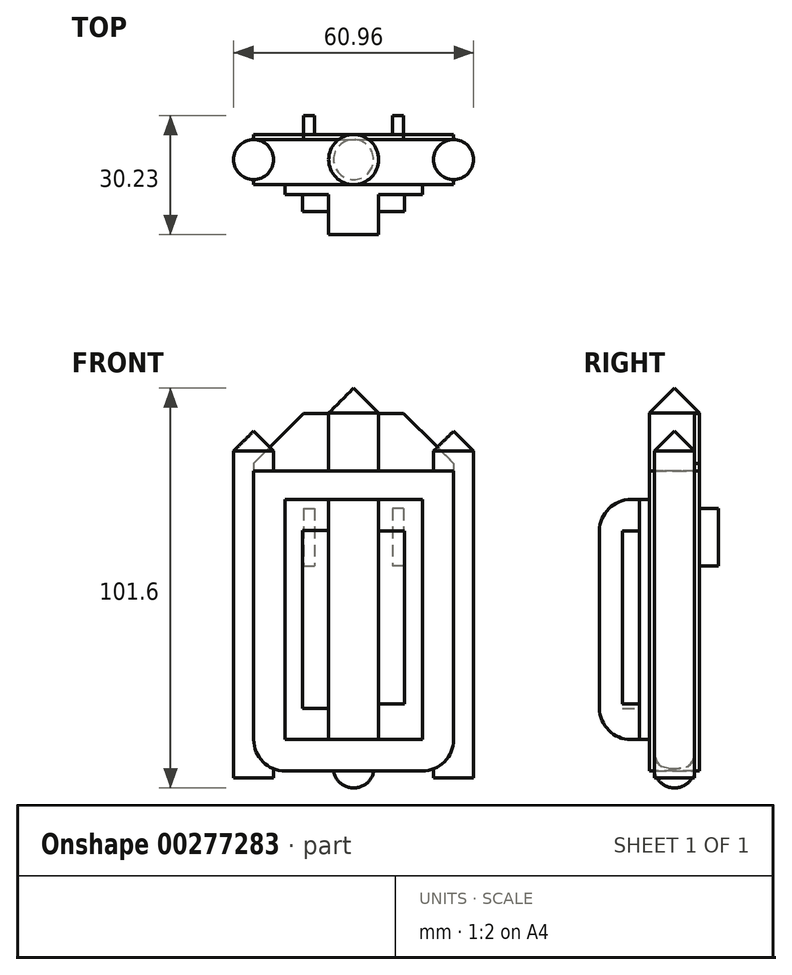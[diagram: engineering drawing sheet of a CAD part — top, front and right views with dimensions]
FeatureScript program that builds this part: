
annotation { "Feature Type Name" : "Feature", "Feature Type Description" : "" }
export const myFeature = defineFeature(function(context is Context, id is Id, definition is map)
    precondition{}
    {
        {
            var Q0;
            Q0=qCreatedBy(makeId("Front.planeOp"),FACE);
            var sketch = newSketch(context, id + "F0", { "sketchPlane" : qUnion([Q0])});
            skLineSegment(sketch, "E0.bottom", {"start": v(-23.73, -37.34) * mm, "end": v(27.07, -37.34) * mm});
            skLineSegment(sketch, "E0.top", {"start": v(-23.73, 38.86) * mm, "end": v(27.07, 38.86) * mm});
            skLineSegment(sketch, "E0.left", {"start": v(-23.73, -37.34) * mm, "end": v(-23.73, 38.86) * mm});
            skLineSegment(sketch, "E0.right", {"start": v(27.07, -37.34) * mm, "end": v(27.07, 38.86) * mm});
            skSolve(sketch);
        }
        {
            var Q0;
            Q0 = qSketchRegion(id + "F0", true);
            extrude(context, id + "F1", {"entities" : qUnion([Q0]), "depth" : 12.7 * mm});
        }
        {
            var Q0;
            Q0=makeQuery(id+"F1.opExtrude","SWEPT_EDGE",EDGE,{"disambiguationData":[OSD([sQuery(id+"F0.wireOp",EDGE,"E0.bottom"),sQuery(id+"F0.wireOp",EDGE,"E0.left")])]});
            var Q1;
            Q1=makeQuery(id+"F1.opExtrude","SWEPT_EDGE",EDGE,{"disambiguationData":[OSD([sQuery(id+"F0.wireOp",EDGE,"E0.bottom"),sQuery(id+"F0.wireOp",EDGE,"E0.right")])]});
            fillet(context, id + "F2", {"entities" : qUnion([Q0, Q1]), "radius" : 7.97 * mm, "tangentPropagation" : true, "allowEdgeOverflow" : false});
        }
        {
            var Q0;
            Q0=makeQuery(id+"F1.opExtrude","CAP_FACE",FACE,{"disambiguationData":[OSD([sQuery(id+"F0.wireOp",EDGE,"E0.bottom"),sQuery(id+"F0.wireOp",EDGE,"E0.top"),sQuery(id+"F0.wireOp",EDGE,"E0.left"),sQuery(id+"F0.wireOp",EDGE,"E0.right")])],"isStart":false});
            var sketch = newSketch(context, id + "F3", { "sketchPlane" : qUnion([Q0])});
            skLineSegment(sketch, "E1", {"start": v(-15.76, -29.36) * mm, "end": v(19.1, -29.36) * mm});
            skLineSegment(sketch, "E2", {"start": v(19.1, -29.36) * mm, "end": v(19.1, 31.64) * mm});
            skLineSegment(sketch, "E3", {"start": v(19.1, 31.64) * mm, "end": v(-15.76, 31.64) * mm});
            skLineSegment(sketch, "E4", {"start": v(-15.76, 31.64) * mm, "end": v(-15.76, -29.36) * mm});
            skSolve(sketch);
        }
        {
            var Q0;
            Q0 = qSketchRegion(id + "F3", true);
            extrude(context, id + "F4", {"entities" : qUnion([Q0]), "operationType" : NewBodyOperationType.ADD, "depth" : 2.54 * mm});
        }
        {
            var Q0;
            Q0=makeQuery(id+"F1.opExtrude","SWEPT_FACE",FACE,{"disambiguationData":[OSD([sQuery(id+"F0.wireOp",EDGE,"E0.top")])]});
            var sketch = newSketch(context, id + "F5", { "sketchPlane" : qUnion([Q0])});
            skCircle(sketch, "E5", {"center": v(-23.73, -6.35) * mm, "radius": 5.08 * mm});
            skPoint(sketch, "E6.centerSnap0", {"position": v(1.67, 0) * mm});
            skCircle(sketch, "E7", {"center": v(27.07, -6.35) * mm, "radius": 5.08 * mm});
            skSolve(sketch);
        }
        {
            var Q0;
            {var subQ0=sQuery(id+"F5.wireOp",EDGE,"E5");var subQ1=makeQuery(id+"F1.opExtrude","SWEPT_EDGE",EDGE,{"disambiguationData":[OSD([sQuery(id+"F0.wireOp",EDGE,"E0.top"),sQuery(id+"F0.wireOp",EDGE,"E0.left")])]});var subQ2=makeQuery(id+"F5.imprint","INTERSECT",VERTEX,{"disambiguationData":[OD(0.0)],"derivedFrom":[subQ1,subQ0]});Q0=makeQuery(id+"F5.imprint","IMPRINT",FACE,{"disambiguationData":[TD([[makeQuery(id+"F5.imprint","IMPRINT",EDGE,{"disambiguationData":[TD([[subQ2,-1.0]])],"derivedFrom":subQ0}),1.0]])]});}
            var Q1;
            {var subQ0=sQuery(id+"F5.wireOp",EDGE,"E7");var subQ1=makeQuery(id+"F1.opExtrude","SWEPT_EDGE",EDGE,{"disambiguationData":[OSD([sQuery(id+"F0.wireOp",EDGE,"E0.top"),sQuery(id+"F0.wireOp",EDGE,"E0.right")])]});var subQ2=makeQuery(id+"F5.imprint","INTERSECT",VERTEX,{"disambiguationData":[OD(0.0)],"derivedFrom":[subQ1,subQ0]});Q1=makeQuery(id+"F5.imprint","IMPRINT",FACE,{"disambiguationData":[TD([[makeQuery(id+"F5.imprint","IMPRINT",EDGE,{"disambiguationData":[TD([[subQ2,1.0]])],"derivedFrom":subQ0}),1.0]])]});}
            var Q2;
            {var subQ0=sQuery(id+"F5.wireOp",EDGE,"E5");var subQ1=makeQuery(id+"F1.opExtrude","SWEPT_EDGE",EDGE,{"disambiguationData":[OSD([sQuery(id+"F0.wireOp",EDGE,"E0.top"),sQuery(id+"F0.wireOp",EDGE,"E0.left")])]});var subQ2=makeQuery(id+"F5.imprint","INTERSECT",VERTEX,{"disambiguationData":[OD(0.0)],"derivedFrom":[subQ1,subQ0]});Q2=makeQuery(id+"F5.imprint","IMPRINT",FACE,{"disambiguationData":[TD([[makeQuery(id+"F5.imprint","IMPRINT",EDGE,{"disambiguationData":[TD([[subQ2,1.0]])],"derivedFrom":subQ0}),1.0]])]});}
            var Q3;
            {var subQ0=sQuery(id+"F5.wireOp",EDGE,"E7");var subQ1=makeQuery(id+"F1.opExtrude","SWEPT_EDGE",EDGE,{"disambiguationData":[OSD([sQuery(id+"F0.wireOp",EDGE,"E0.top"),sQuery(id+"F0.wireOp",EDGE,"E0.right")])]});var subQ2=makeQuery(id+"F5.imprint","INTERSECT",VERTEX,{"disambiguationData":[OD(0.0)],"derivedFrom":[subQ1,subQ0]});Q3=makeQuery(id+"F5.imprint","IMPRINT",FACE,{"disambiguationData":[TD([[makeQuery(id+"F5.imprint","IMPRINT",EDGE,{"disambiguationData":[TD([[subQ2,-1.0]])],"derivedFrom":subQ0}),1.0]])]});}
            extrude(context, id + "F6", {"entities" : qUnion([Q0, Q1, Q2, Q3]), "operationType" : NewBodyOperationType.ADD, "oppositeDirection" : true, "depth" : 77.98 * mm});
        }
        {
            var Q0;
            Q0=makeQuery(id+"F6.boolean.opBoolean","MERGE",FACE,{"derivedFrom":[makeQuery(id+"F1.opExtrude","SWEPT_FACE",FACE,{"disambiguationData":[OSD([sQuery(id+"F0.wireOp",EDGE,"E0.top")])]}),makeQuery(id+"F6.opExtrude","CAP_FACE",FACE,{"disambiguationData":[OSD([sQuery(id+"F5.wireOp",EDGE,"E5")])],"isStart":true}),makeQuery(id+"F6.opExtrude","CAP_FACE",FACE,{"disambiguationData":[OSD([sQuery(id+"F5.wireOp",EDGE,"E7")])],"isStart":true})]});
            var sketch = newSketch(context, id + "F7", { "sketchPlane" : qUnion([Q0])});
            skCircle(sketch, "E8", {"center": v(1.67, -6.35) * mm, "radius": 6.35 * mm});
            skPoint(sketch, "E8.centerSnap0", {"position": v(1.67, 0) * mm});
            skPoint(sketch, "E8.centerSnap1", {"position": v(-28.8, -6.35) * mm});
            skSolve(sketch);
        }
        {
            var Q0;
            Q0 = qSketchRegion(id + "F7", true);
            extrude(context, id + "F8", {"entities" : qUnion([Q0]), "operationType" : NewBodyOperationType.ADD, "depth" : 21.08 * mm});
        }
        {
            var Q0;
            Q0=makeQuery(id+"F8.opExtrude","CAP_EDGE",EDGE,{"disambiguationData":[OSD([sQuery(id+"F7.wireOp",EDGE,"E8")])],"isStart":false});
            chamfer(context, id + "F9", {"entities" : qUnion([Q0]), "width" : 6.35 * mm, "tangentPropagation" : true});
        }
        {
            var Q0;
            Q0=makeQuery(id+"F4.opExtrude","CAP_FACE",FACE,{"disambiguationData":[OSD([sQuery(id+"F3.wireOp",EDGE,"E1"),sQuery(id+"F3.wireOp",EDGE,"E2"),sQuery(id+"F3.wireOp",EDGE,"E3"),sQuery(id+"F3.wireOp",EDGE,"E4")])],"isStart":false});
            var sketch = newSketch(context, id + "F10", { "sketchPlane" : qUnion([Q0])});
            skLineSegment(sketch, "E9", {"start": v(1.67, 31.64) * mm, "end": v(-4.68, 31.64) * mm});
            skLineSegment(sketch, "E10", {"start": v(1.67, 31.64) * mm, "end": v(8.02, 31.64) * mm});
            skLineSegment(sketch, "E11", {"start": v(-4.68, 31.64) * mm, "end": v(-4.68, -29.36) * mm});
            skLineSegment(sketch, "E12", {"start": v(-4.68, -29.36) * mm, "end": v(8.02, -29.36) * mm});
            skLineSegment(sketch, "E13", {"start": v(8.02, -29.36) * mm, "end": v(8.02, 31.64) * mm});
            skSolve(sketch);
        }
        {
            var Q0;
            Q0 = qSketchRegion(id + "F10", true);
            extrude(context, id + "F11", {"entities" : qUnion([Q0]), "operationType" : NewBodyOperationType.ADD, "depth" : 10.16 * mm});
        }
        {
            var Q0;
            Q0=makeQuery(id+"F11.opExtrude","CAP_EDGE",EDGE,{"disambiguationData":[OSD([sQuery(id+"F10.wireOp",EDGE,"E9"),sQuery(id+"F10.wireOp",EDGE,"E10")])],"isStart":false});
            var Q1;
            Q1=makeQuery(id+"F11.opExtrude","CAP_EDGE",EDGE,{"disambiguationData":[OSD([sQuery(id+"F10.wireOp",EDGE,"E12")])],"isStart":false});
            fillet(context, id + "F12", {"entities" : qUnion([Q0, Q1]), "radius" : 7.97 * mm, "tangentPropagation" : true, "allowEdgeOverflow" : false});
        }
        {
            var Q0;
            Q0 = qSketchRegion(id + "F5", true);
            extrude(context, id + "F13", {"entities" : qUnion([Q0]), "operationType" : NewBodyOperationType.ADD, "depth" : 10.16 * mm});
        }
        {
            var Q0;
            Q0=makeQuery(id+"F13.opExtrude","CAP_EDGE",EDGE,{"disambiguationData":[OSD([sQuery(id+"F5.wireOp",EDGE,"E5")])],"isStart":false});
            var Q1;
            Q1=makeQuery(id+"F13.opExtrude","CAP_EDGE",EDGE,{"disambiguationData":[OSD([sQuery(id+"F5.wireOp",EDGE,"E7")])],"isStart":false});
            chamfer(context, id + "F14", {"entities" : qUnion([Q0, Q1]), "width" : 5.08 * mm, "tangentPropagation" : true});
        }
        {
            var Q0;
            Q0=makeQuery(id+"F1.opExtrude","SWEPT_FACE",FACE,{"disambiguationData":[OSD([sQuery(id+"F0.wireOp",EDGE,"E0.bottom")])]});
            var sketch = newSketch(context, id + "F15", { "sketchPlane" : qUnion([Q0])});
            skCircle(sketch, "E14", {"center": v(1.67, 6.35) * mm, "radius": 5.08 * mm});
            skPoint(sketch, "E14.centerSnap0", {"position": v(-15.76, 6.35) * mm});
            skPoint(sketch, "E14.centerSnap1", {"position": v(1.67, 12.7) * mm});
            skSolve(sketch);
        }
        {
            var Q0;
            Q0=makeQuery(id+"F15.imprint","IMPRINT",FACE,{"disambiguationData":[TD([[makeQuery(id+"F15.imprint","IMPRINT",EDGE,{"derivedFrom":sQuery(id+"F15.wireOp",EDGE,"E14")}),1.0]])]});
            extrude(context, id + "F16", {"entities" : qUnion([Q0]), "operationType" : NewBodyOperationType.ADD, "depth" : 4.32 * mm});
        }
        {
            var Q0;
            Q0=makeQuery(id+"F16.opExtrude","CAP_EDGE",EDGE,{"disambiguationData":[OSD([sQuery(id+"F15.wireOp",EDGE,"E14")])],"isStart":false});
            fillet(context, id + "F17", {"entities" : qUnion([Q0]), "radius" : 5.08 * mm, "tangentPropagation" : true, "allowEdgeOverflow" : false});
        }
        {
            var Q0;
            {var subQ0=sQuery(id+"F0.wireOp",EDGE,"E0.left");var subQ1=sQuery(id+"F0.wireOp",EDGE,"E0.top");var subQ2=makeQuery(id+"F1.opExtrude","SWEPT_FACE",FACE,{"disambiguationData":[OSD([subQ1])]});var subQ5=sQuery(id+"F5.wireOp",EDGE,"E5");var subQ6=makeQuery(id+"F6.opExtrude","CAP_FACE",FACE,{"disambiguationData":[OSD([subQ5])],"isStart":true});var subQ7=makeQuery(id+"F6.opExtrude","CAP_FACE",FACE,{"disambiguationData":[OSD([sQuery(id+"F5.wireOp",EDGE,"E7")])],"isStart":true});Q0=makeQuery(id+"F8.boolean.opBoolean","SPLIT",FACE,{"disambiguationData":[TD([makeQuery(id+"F1.opExtrude","SWEPT_FACE",FACE,{"disambiguationData":[OSD([subQ0])]})])],"derivedFrom":makeQuery(id+"F6.boolean.opBoolean","MERGE",FACE,{"derivedFrom":[subQ2,subQ6,subQ7]})});}
            var sketch = newSketch(context, id + "F18", { "sketchPlane" : qUnion([Q0])});
            skLineSegment(sketch, "E15", {"start": v(-23.73, 0) * mm, "end": v(1.67, 0) * mm});
            skLineSegment(sketch, "E16", {"start": v(1.67, 0) * mm, "end": v(27.07, 0) * mm});
            skLineSegment(sketch, "E17", {"start": v(-23.73, 0) * mm, "end": v(-23.73, -1.27) * mm});
            skLineSegment(sketch, "E18", {"start": v(-23.73, -1.27) * mm, "end": v(27.07, -1.27) * mm});
            skLineSegment(sketch, "E19", {"start": v(27.07, -1.27) * mm, "end": v(27.07, 0) * mm});
            skSolve(sketch);
        }
        {
            var Q0;
            Q0 = qSketchRegion(id + "F18", true);
            extrude(context, id + "F19", {"entities" : qUnion([Q0]), "depth" : 14.66 * mm});
        }
        {
            var Q0;
            Q0=makeQuery(id+"F19.opExtrude","CAP_EDGE",EDGE,{"disambiguationData":[OSD([sQuery(id+"F18.wireOp",EDGE,"E19")])],"isStart":false});
            var Q1;
            Q1=makeQuery(id+"F19.opExtrude","CAP_EDGE",EDGE,{"disambiguationData":[OSD([sQuery(id+"F18.wireOp",EDGE,"E17")])],"isStart":false});
            chamfer(context, id + "F20", {"entities" : qUnion([Q0, Q1]), "width" : 12.7 * mm, "tangentPropagation" : true});
        }
        {
            var Q0;
            {var subQ0=sQuery(id+"F3.wireOp",EDGE,"E3");var subQ1=sQuery(id+"F3.wireOp",EDGE,"E2");var subQ2=sQuery(id+"F3.wireOp",EDGE,"E1");Q0=makeQuery(id+"F11.boolean.opBoolean","SPLIT",FACE,{"disambiguationData":[TD([makeQuery(id+"F4.opExtrude","SWEPT_FACE",FACE,{"disambiguationData":[OSD([subQ1])]})])],"derivedFrom":makeQuery(id+"F4.opExtrude","CAP_FACE",FACE,{"disambiguationData":[OSD([subQ2,subQ1,subQ0,sQuery(id+"F3.wireOp",EDGE,"E4")])],"isStart":false})});}
            var sketch = newSketch(context, id + "F21", { "sketchPlane" : qUnion([Q0])});
            skLineSegment(sketch, "E20.bottom", {"start": v(8.02, 23.6) * mm, "end": v(14.63, 23.6) * mm});
            skLineSegment(sketch, "E20.top", {"start": v(8.02, -20.33) * mm, "end": v(14.63, -20.33) * mm});
            skLineSegment(sketch, "E20.left", {"start": v(8.02, 23.6) * mm, "end": v(8.02, -20.33) * mm});
            skLineSegment(sketch, "E20.right", {"start": v(14.63, 23.6) * mm, "end": v(14.63, -20.33) * mm});
            skSolve(sketch);
        }
        {
            var Q0;
            Q0=makeQuery(id+"F21.imprint","IMPRINT",FACE,{"disambiguationData":[TD([[makeQuery(id+"F21.imprint","IMPRINT",EDGE,{"derivedFrom":sQuery(id+"F21.wireOp",EDGE,"E20.bottom")}),-1.0]])]});
            extrude(context, id + "F22", {"entities" : qUnion([Q0]), "operationType" : NewBodyOperationType.ADD, "depth" : 4.32 * mm});
        }
        {
            var Q0;
            {var subQ0=sQuery(id+"F3.wireOp",EDGE,"E4");var subQ1=sQuery(id+"F3.wireOp",EDGE,"E3");var subQ2=sQuery(id+"F3.wireOp",EDGE,"E1");Q0=makeQuery(id+"F11.boolean.opBoolean","SPLIT",FACE,{"disambiguationData":[TD([makeQuery(id+"F4.opExtrude","SWEPT_FACE",FACE,{"disambiguationData":[OSD([subQ0])]})])],"derivedFrom":makeQuery(id+"F4.opExtrude","CAP_FACE",FACE,{"disambiguationData":[OSD([subQ2,sQuery(id+"F3.wireOp",EDGE,"E2"),subQ1,subQ0])],"isStart":false})});}
            var sketch = newSketch(context, id + "F23", { "sketchPlane" : qUnion([Q0])});
            skLineSegment(sketch, "E21.bottom", {"start": v(-4.68, 23.73) * mm, "end": v(-11.28, 23.73) * mm});
            skLineSegment(sketch, "E21.top", {"start": v(-4.68, -21.43) * mm, "end": v(-11.28, -21.43) * mm});
            skLineSegment(sketch, "E21.left", {"start": v(-4.68, 23.73) * mm, "end": v(-4.68, -21.43) * mm});
            skLineSegment(sketch, "E21.right", {"start": v(-11.28, 23.73) * mm, "end": v(-11.28, -21.43) * mm});
            skSolve(sketch);
        }
        {
            var Q0;
            Q0 = qSketchRegion(id + "F23", true);
            extrude(context, id + "F24", {"entities" : qUnion([Q0]), "operationType" : NewBodyOperationType.ADD, "depth" : 4.32 * mm});
        }
        {
            var Q0;
            Q0=makeQuery(id+"F1.opExtrude","CAP_FACE",FACE,{"disambiguationData":[OSD([sQuery(id+"F0.wireOp",EDGE,"E0.bottom"),sQuery(id+"F0.wireOp",EDGE,"E0.top"),sQuery(id+"F0.wireOp",EDGE,"E0.left"),sQuery(id+"F0.wireOp",EDGE,"E0.right")])],"isStart":true});
            var sketch = newSketch(context, id + "F25", { "sketchPlane" : qUnion([Q0])});
            skPoint(sketch, "E22.firstSnap0", {"position": v(-14.37, 38.86) * mm});
            skLineSegment(sketch, "E22.bottom", {"start": v(-14.37, 29.33) * mm, "end": v(-11.58, 29.33) * mm});
            skLineSegment(sketch, "E22.top", {"start": v(-14.37, 14.8) * mm, "end": v(-11.58, 14.8) * mm});
            skLineSegment(sketch, "E22.left", {"start": v(-14.37, 29.33) * mm, "end": v(-14.37, 14.8) * mm});
            skLineSegment(sketch, "E22.right", {"start": v(-11.58, 29.33) * mm, "end": v(-11.58, 14.8) * mm});
            skLineSegment(sketch, "E23", {"start": v(-1.67, 38.86) * mm, "end": v(-1.67, -37.34) * mm, "construction": true});
            skLineSegment(sketch, "E24.MirrorCS", {"start": v(8.23, 29.33) * mm, "end": v(8.23, 14.8) * mm});
            skLineSegment(sketch, "E25.MirrorCS", {"start": v(11.03, 29.33) * mm, "end": v(8.23, 29.33) * mm});
            skLineSegment(sketch, "E26.MirrorCS", {"start": v(11.03, 29.33) * mm, "end": v(11.03, 14.8) * mm});
            skLineSegment(sketch, "E27.MirrorCS", {"start": v(11.03, 14.8) * mm, "end": v(8.23, 14.8) * mm});
            skSolve(sketch);
        }
        {
            var Q0;
            Q0 = qSketchRegion(id + "F25", true);
            extrude(context, id + "F26", {"entities" : qUnion([Q0]), "operationType" : NewBodyOperationType.ADD, "depth" : 4.83 * mm});
        }
    });
